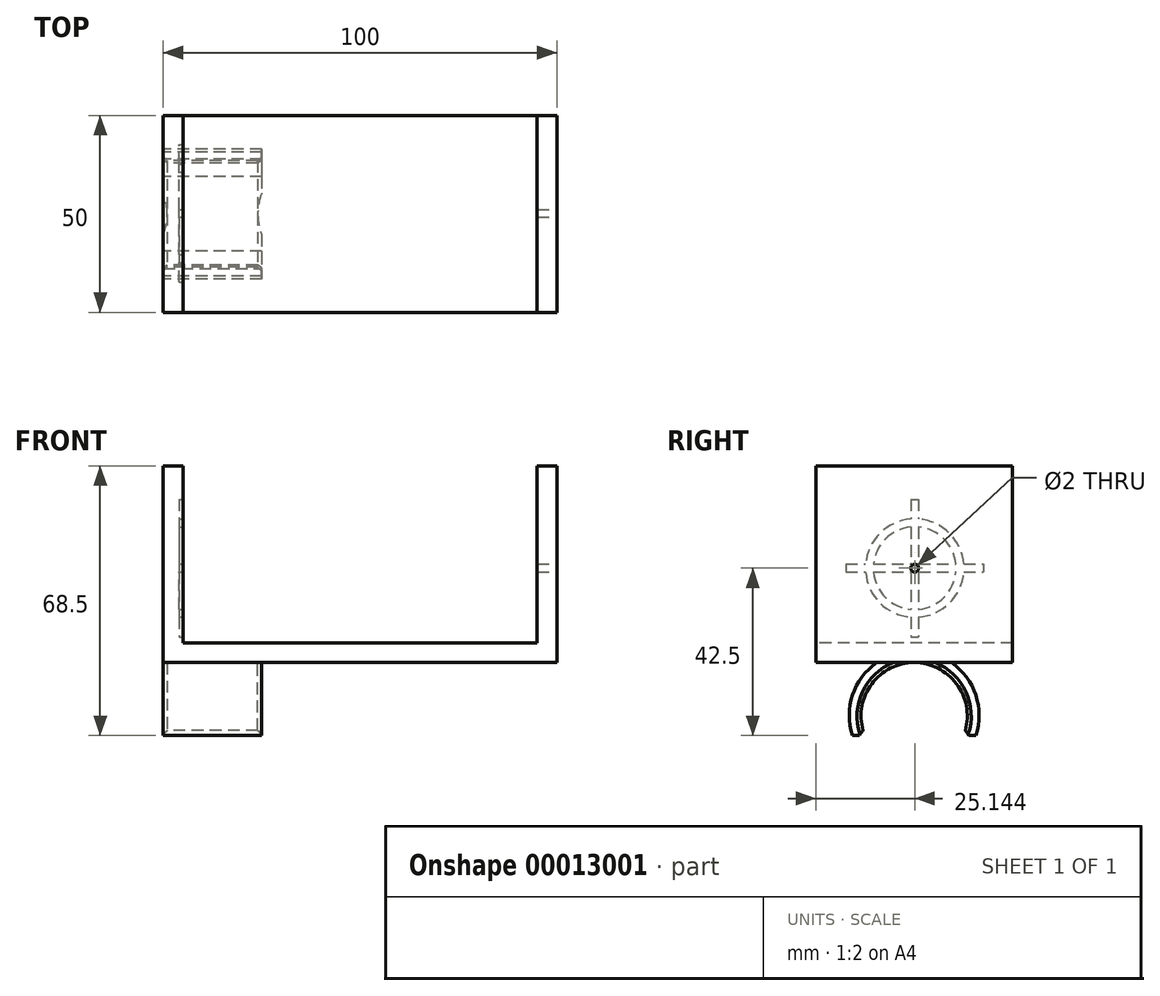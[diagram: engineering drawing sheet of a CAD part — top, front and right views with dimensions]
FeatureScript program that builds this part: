
annotation { "Feature Type Name" : "Feature", "Feature Type Description" : "" }
export const myFeature = defineFeature(function(context is Context, id is Id, definition is map)
    precondition{}
    {
        {
            var Q0;
            Q0=qCreatedBy(makeId("Right.planeOp"),FACE);
            var sketch = newSketch(context, id + "F0", { "sketchPlane" : qUnion([Q0])});
            skCircle(sketch, "E0", {"center": v(0, 0) * mm, "radius": 16.5 * mm});
            skCircle(sketch, "E1", {"center": v(0, 0) * mm, "radius": 13.5 * mm});
            skSolve(sketch);
        }
        {
            var Q0;
            Q0 = qSketchRegion(id + "F0", true);
            extrude(context, id + "F1", {"entities" : qUnion([Q0]), "depth" : 25 * mm});
        }
        {
            var Q0;
            Q0=qCreatedBy(makeId("Right.planeOp"),FACE);
            var sketch = newSketch(context, id + "F11", { "sketchPlane" : qUnion([Q0])});
            skLineSegment(sketch, "E2.bottom", {"start": v(-20, -5) * mm, "end": v(20, -5) * mm});
            skLineSegment(sketch, "E2.top", {"start": v(-20, -25) * mm, "end": v(20, -25) * mm});
            skLineSegment(sketch, "E2.left", {"start": v(-20, -5) * mm, "end": v(-20, -25) * mm});
            skLineSegment(sketch, "E2.right", {"start": v(20, -5) * mm, "end": v(20, -25) * mm});
            skSolve(sketch);
        }
        {
            var Q0;
            Q0 = qSketchRegion(id + "F11", true);
            extrude(context, id + "F2", {"entities" : qUnion([Q0]), "operationType" : NewBodyOperationType.REMOVE, "endBound" : BoundingType.SYMMETRIC, "oppositeDirection" : true, "depth" : 50 * mm});
        }
        {
            var Q0;
            Q0=makeQuery(id+"F1.opExtrude","SWEPT_FACE",FACE,{"disambiguationData":[OSD([sQuery(id+"F0.wireOp",EDGE,"E1")])]});
            chamfer(context, id + "F12", {"entities" : qUnion([Q0]), "width" : 1 * mm, "tangentPropagation" : true});
        }
        {
            var Q0;
            Q0=qCreatedBy(makeId("Right.planeOp"),FACE);
            var sketch = newSketch(context, id + "F3", { "sketchPlane" : qUnion([Q0])});
            skLineSegment(sketch, "E3.bottom", {"start": v(-25, 18.5) * mm, "end": v(25, 18.5) * mm});
            skLineSegment(sketch, "E3.top", {"start": v(-25, 13.5) * mm, "end": v(25, 13.5) * mm});
            skLineSegment(sketch, "E3.left", {"start": v(-25, 18.5) * mm, "end": v(-25, 13.5) * mm});
            skLineSegment(sketch, "E3.right", {"start": v(25, 18.5) * mm, "end": v(25, 13.5) * mm});
            skSolve(sketch);
        }
        {
            var Q0;
            Q0 = qSketchRegion(id + "F3", true);
            extrude(context, id + "F4", {"entities" : qUnion([Q0]), "operationType" : NewBodyOperationType.ADD, "depth" : 100 * mm});
        }
        {
            var Q0;
            Q0=makeQuery(id+"F4.opExtrude","CAP_FACE",FACE,{"disambiguationData":[OSD([sQuery(id+"F3.wireOp",EDGE,"E3.bottom"),sQuery(id+"F3.wireOp",EDGE,"E3.top"),sQuery(id+"F3.wireOp",EDGE,"E3.left"),sQuery(id+"F3.wireOp",EDGE,"E3.right")])],"isStart":false});
            var sketch = newSketch(context, id + "F13", { "sketchPlane" : qUnion([Q0])});
            skLineSegment(sketch, "E4.bottom", {"start": v(-25, 63.5) * mm, "end": v(25, 63.5) * mm});
            skLineSegment(sketch, "E4.top", {"start": v(-25, 13.5) * mm, "end": v(25, 13.5) * mm});
            skLineSegment(sketch, "E4.left", {"start": v(-25, 63.5) * mm, "end": v(-25, 13.5) * mm});
            skLineSegment(sketch, "E4.right", {"start": v(25, 63.5) * mm, "end": v(25, 13.5) * mm});
            skSolve(sketch);
        }
        {
            var Q0;
            Q0 = qSketchRegion(id + "F13", true);
            extrude(context, id + "F5", {"entities" : qUnion([Q0]), "operationType" : NewBodyOperationType.ADD, "oppositeDirection" : true, "depth" : 5 * mm});
        }
        {
            var Q0;
            Q0=makeQuery(id+"F4.opExtrude","CAP_FACE",FACE,{"disambiguationData":[OSD([sQuery(id+"F3.wireOp",EDGE,"E3.bottom"),sQuery(id+"F3.wireOp",EDGE,"E3.top"),sQuery(id+"F3.wireOp",EDGE,"E3.left"),sQuery(id+"F3.wireOp",EDGE,"E3.right")])],"isStart":true});
            var sketch = newSketch(context, id + "F6", { "sketchPlane" : qUnion([Q0])});
            skLineSegment(sketch, "E5.bottom", {"start": v(-25, 63.5) * mm, "end": v(25, 63.5) * mm});
            skLineSegment(sketch, "E5.top", {"start": v(-25, 13.5) * mm, "end": v(25, 13.5) * mm});
            skLineSegment(sketch, "E5.left", {"start": v(-25, 63.5) * mm, "end": v(-25, 13.5) * mm});
            skLineSegment(sketch, "E5.right", {"start": v(25, 63.5) * mm, "end": v(25, 13.5) * mm});
            skSolve(sketch);
        }
        {
            var Q0;
            Q0 = qSketchRegion(id + "F6", true);
            extrude(context, id + "F14", {"entities" : qUnion([Q0]), "operationType" : NewBodyOperationType.ADD, "oppositeDirection" : true, "depth" : 5 * mm});
        }
        {
            var Q0;
            Q0=makeQuery(id+"F5.boolean.opBoolean","MERGE",FACE,{"derivedFrom":[makeQuery(id+"F4.opExtrude","CAP_FACE",FACE,{"disambiguationData":[OSD([sQuery(id+"F3.wireOp",EDGE,"E3.bottom"),sQuery(id+"F3.wireOp",EDGE,"E3.top"),sQuery(id+"F3.wireOp",EDGE,"E3.left"),sQuery(id+"F3.wireOp",EDGE,"E3.right")])],"isStart":false}),makeQuery(id+"F5.opExtrude","CAP_FACE",FACE,{"disambiguationData":[OSD([sQuery(id+"F13.wireOp",EDGE,"E4.bottom"),sQuery(id+"F13.wireOp",EDGE,"E4.top"),sQuery(id+"F13.wireOp",EDGE,"E4.left"),sQuery(id+"F13.wireOp",EDGE,"E4.right")])],"isStart":true})]});
            var sketch = newSketch(context, id + "F7", { "sketchPlane" : qUnion([Q0])});
            skCircle(sketch, "E6", {"center": v(0.14, 37.5) * mm, "radius": 1 * mm});
            skSolve(sketch);
        }
        {
            var Q0;
            Q0 = qSketchRegion(id + "F7", true);
            extrude(context, id + "F8", {"entities" : qUnion([Q0]), "operationType" : NewBodyOperationType.REMOVE, "oppositeDirection" : true, "depth" : 25 * mm});
        }
        {
            var Q0;
            Q0=makeQuery(id+"F14.opExtrude","CAP_FACE",FACE,{"disambiguationData":[OSD([sQuery(id+"F6.wireOp",EDGE,"E5.bottom"),sQuery(id+"F6.wireOp",EDGE,"E5.top"),sQuery(id+"F6.wireOp",EDGE,"E5.left"),sQuery(id+"F6.wireOp",EDGE,"E5.right")])],"isStart":false});
            var sketch = newSketch(context, id + "F9", { "sketchPlane" : qUnion([Q0])});
            skArc(sketch, "E7", {"start": v(-0.86, 49.96) * mm, "mid": v(-8.7, 46.34) * mm, "end": v(-12.32, 38.5) * mm});
            skArc(sketch, "E8", {"start": v(-0.86, 47.95) * mm, "mid": v(-7.28, 44.92) * mm, "end": v(-10.3, 38.5) * mm});
            skLineSegment(sketch, "E9.bottom", {"start": v(-0.86, 55) * mm, "end": v(1.14, 55) * mm});
            skLineSegment(sketch, "E9.top", {"start": v(-0.86, 20) * mm, "end": v(1.14, 20) * mm});
            skLineSegment(sketch, "E9.left", {"start": v(-0.86, 55) * mm, "end": v(-0.86, 49.96) * mm});
            skLineSegment(sketch, "E9.right", {"start": v(1.14, 55) * mm, "end": v(1.14, 49.96) * mm});
            skLineSegment(sketch, "E10.bottom", {"start": v(-17.36, 38.5) * mm, "end": v(-12.32, 38.5) * mm});
            skLineSegment(sketch, "E10.top", {"start": v(-17.36, 36.5) * mm, "end": v(-12.32, 36.5) * mm});
            skLineSegment(sketch, "E10.left", {"start": v(-17.36, 38.5) * mm, "end": v(-17.36, 36.5) * mm});
            skLineSegment(sketch, "E10.right", {"start": v(17.64, 38.5) * mm, "end": v(17.64, 36.5) * mm});
            skLineSegment(sketch, "E11.trimOffspring", {"start": v(1.14, 38.5) * mm, "end": v(10.6, 38.5) * mm});
            skLineSegment(sketch, "E12.trimOffspring", {"start": v(1.14, 36.5) * mm, "end": v(1.14, 27.05) * mm});
            skLineSegment(sketch, "E13.trimOffspring", {"start": v(-0.86, 36.5) * mm, "end": v(-0.86, 27.05) * mm});
            skLineSegment(sketch, "E14.trimOffspring", {"start": v(1.14, 36.5) * mm, "end": v(10.6, 36.5) * mm});
            skLineSegment(sketch, "E15.trimOffspring", {"start": v(-0.86, 47.95) * mm, "end": v(-0.86, 38.5) * mm});
            skLineSegment(sketch, "E16.trimOffspring", {"start": v(1.14, 47.95) * mm, "end": v(1.14, 38.5) * mm});
            skArc(sketch, "E17.trimOffspring", {"start": v(12.6, 38.5) * mm, "mid": v(8.98, 46.34) * mm, "end": v(1.14, 49.96) * mm});
            skLineSegment(sketch, "E18.trimOffspring", {"start": v(12.6, 38.5) * mm, "end": v(17.64, 38.5) * mm});
            skArc(sketch, "E19.trimOffspring", {"start": v(10.6, 38.5) * mm, "mid": v(7.57, 44.92) * mm, "end": v(1.14, 47.95) * mm});
            skLineSegment(sketch, "E20.trimOffspring", {"start": v(12.6, 36.5) * mm, "end": v(17.64, 36.5) * mm});
            skArc(sketch, "E21.trimOffspring", {"start": v(-10.3, 36.5) * mm, "mid": v(-7.28, 30.08) * mm, "end": v(-0.86, 27.05) * mm});
            skLineSegment(sketch, "E22.trimOffspring", {"start": v(-10.3, 38.5) * mm, "end": v(-0.86, 38.5) * mm});
            skArc(sketch, "E23.trimOffspring", {"start": v(-12.32, 36.5) * mm, "mid": v(-8.7, 28.66) * mm, "end": v(-0.86, 25.04) * mm});
            skLineSegment(sketch, "E24.trimOffspring", {"start": v(-10.3, 36.5) * mm, "end": v(-0.86, 36.5) * mm});
            skArc(sketch, "E25.trimOffspring", {"start": v(1.14, 25.04) * mm, "mid": v(8.98, 28.66) * mm, "end": v(12.6, 36.5) * mm});
            skArc(sketch, "E26.trimOffspring", {"start": v(1.14, 27.05) * mm, "mid": v(7.57, 30.08) * mm, "end": v(10.6, 36.5) * mm});
            skLineSegment(sketch, "E27.trimOffspring", {"start": v(1.14, 25.04) * mm, "end": v(1.14, 20) * mm});
            skLineSegment(sketch, "E28.trimOffspring", {"start": v(-0.86, 25.04) * mm, "end": v(-0.86, 20) * mm});
            skSolve(sketch);
        }
        {
            var Q0;
            Q0 = qSketchRegion(id + "F9", true);
            extrude(context, id + "F10", {"entities" : qUnion([Q0]), "operationType" : NewBodyOperationType.REMOVE, "oppositeDirection" : true, "depth" : 1 * mm});
        }
    });
